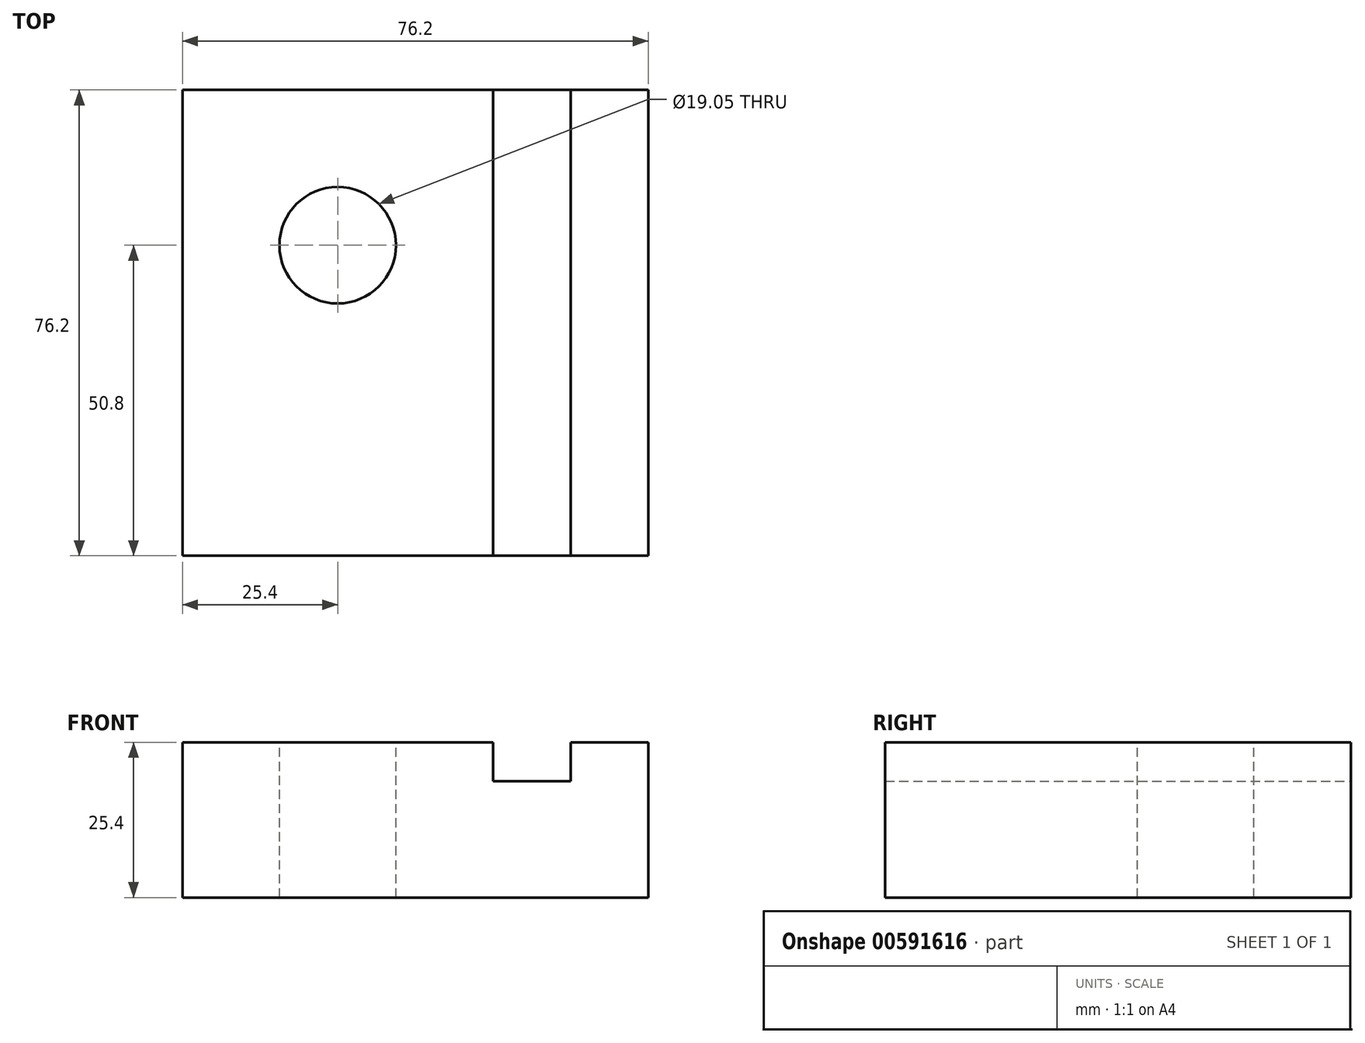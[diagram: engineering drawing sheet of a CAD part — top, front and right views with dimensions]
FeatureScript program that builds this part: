
annotation { "Feature Type Name" : "Feature", "Feature Type Description" : "" }
export const myFeature = defineFeature(function(context is Context, id is Id, definition is map)
    precondition{}
    {
        {
            var Q0;
            Q0=qCreatedBy(makeId("Front.planeOp"),FACE);
            var sketch = newSketch(context, id + "F0", { "sketchPlane" : qUnion([Q0])});
            skLineSegment(sketch, "E0.bottom", {"start": v(-38.1, 12.7) * mm, "end": v(38.1, 12.7) * mm});
            skLineSegment(sketch, "E0.top", {"start": v(-38.1, -12.7) * mm, "end": v(38.1, -12.7) * mm});
            skLineSegment(sketch, "E0.left", {"start": v(-38.1, 12.7) * mm, "end": v(-38.1, -12.7) * mm});
            skLineSegment(sketch, "E0.right", {"start": v(38.1, 12.7) * mm, "end": v(38.1, -12.7) * mm});
            skPoint(sketch, "E0.middle", {"position": v(0, 0) * mm});
            skLineSegment(sketch, "E1", {"start": v(25.4, 12.7) * mm, "end": v(25.4, 6.35) * mm});
            skLineSegment(sketch, "E2", {"start": v(25.4, 6.35) * mm, "end": v(12.7, 6.35) * mm});
            skLineSegment(sketch, "E3", {"start": v(12.7, 6.35) * mm, "end": v(12.7, 12.7) * mm});
            skSolve(sketch);
        }
        {
            var Q0;
            Q0=makeQuery(id+"F0.imprint","IMPRINT",FACE,{"disambiguationData":[TD([[makeQuery(id+"F0.imprint","IMPRINT",EDGE,{"derivedFrom":sQuery(id+"F0.wireOp",EDGE,"E0.top")}),1.0]])]});
            extrude(context, id + "F1", {"entities" : qUnion([Q0]), "depth" : 76.2 * mm, "offsetDistance" : 25.4 * mm});
        }
        {
            var Q0;
            {var subQ0=sQuery(id+"F0.wireOp",EDGE,"E0.bottom");Q0=makeQuery(id+"F1.opExtrude","SWEPT_FACE",FACE,{"disambiguationData":[OSD([subQ0]),TDD([makeQuery(id+"F0.imprint","IMPRINT",EDGE,{"disambiguationData":[TD([[makeQuery(id+"F0.imprint","INTERSECT",VERTEX,{"derivedFrom":[subQ0,sQuery(id+"F0.wireOp",EDGE,"E0.left")]}),-1.0]])],"derivedFrom":subQ0})])]});}
            var sketch = newSketch(context, id + "F2", { "sketchPlane" : qUnion([Q0])});
            skCircle(sketch, "E4", {"center": v(-12.7, -25.4) * mm, "radius": 9.53 * mm});
            skSolve(sketch);
        }
        {
            var Q0;
            Q0=makeQuery(id+"F2.imprint","IMPRINT",FACE,{"disambiguationData":[TD([[makeQuery(id+"F2.imprint","IMPRINT",EDGE,{"derivedFrom":sQuery(id+"F2.wireOp",EDGE,"E4")}),1.0]])]});
            extrude(context, id + "F3", {"entities" : qUnion([Q0]), "operationType" : NewBodyOperationType.REMOVE, "oppositeDirection" : true, "depth" : 25.4 * mm, "offsetDistance" : 25.4 * mm});
        }
    });
